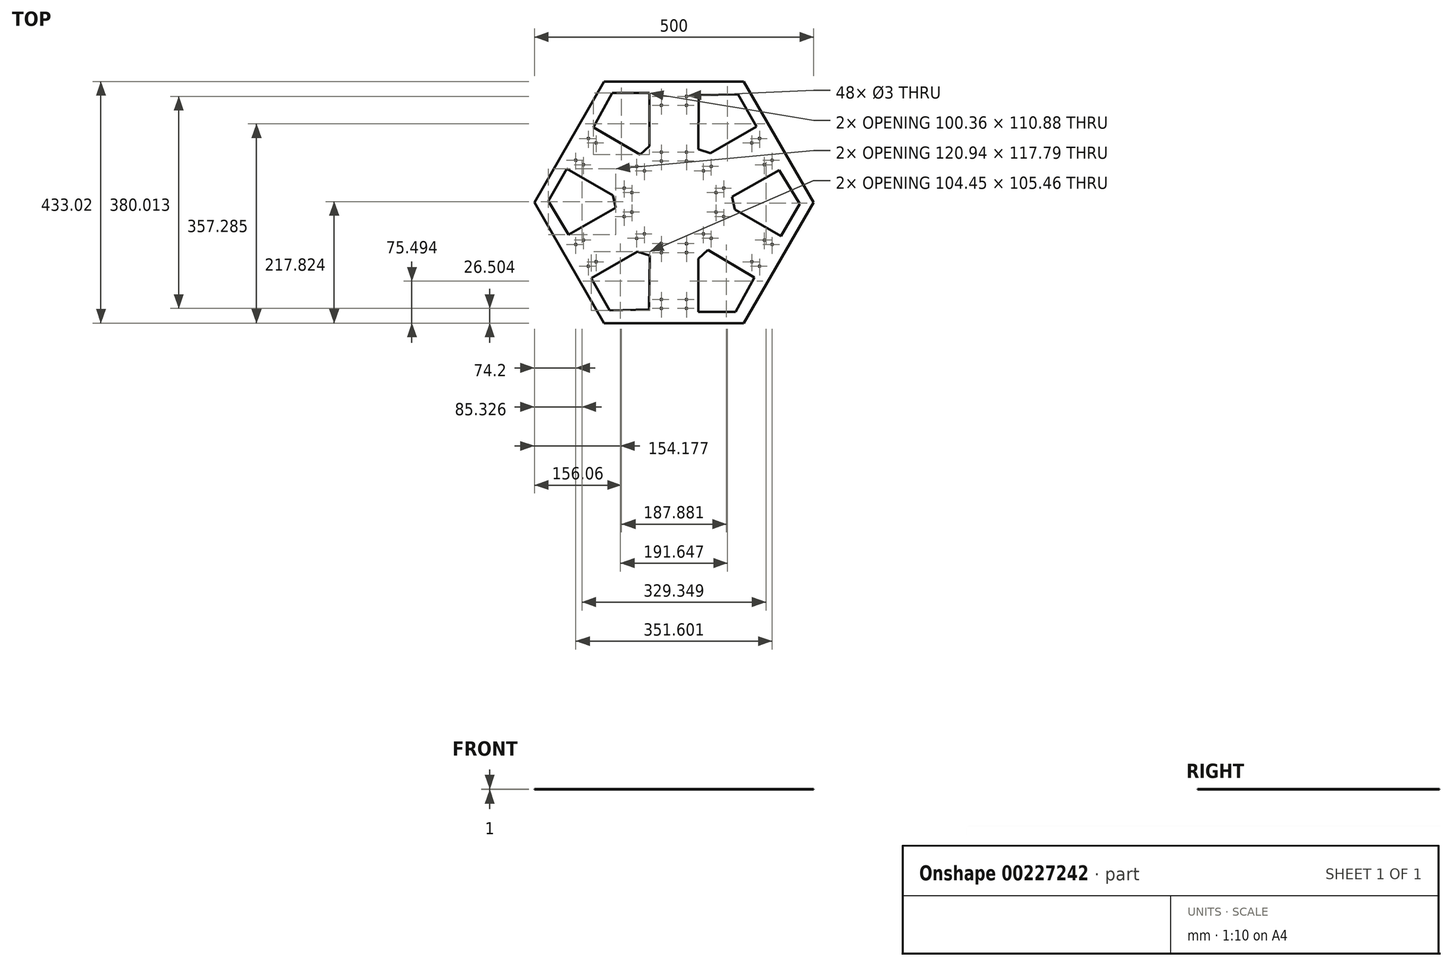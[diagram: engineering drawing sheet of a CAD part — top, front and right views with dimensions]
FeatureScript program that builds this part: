
annotation { "Feature Type Name" : "Feature", "Feature Type Description" : "" }
export const myFeature = defineFeature(function(context is Context, id is Id, definition is map)
    precondition{}
    {
        {
            var Q0;
            Q0=qCreatedBy(makeId("Top.planeOp"),FACE);
            var sketch = newSketch(context, id + "F0", { "sketchPlane" : qUnion([Q0])});
            skCircle(sketch, "E0.cCircle", {"center": v(0, 0) * mm, "radius": 250 * mm, "construction": true});
            skLineSegment(sketch, "E0.0", {"start": v(250, 0) * mm, "end": v(125, -216.5) * mm});
            skLineSegment(sketch, "E0.1", {"start": v(125, -216.5) * mm, "end": v(-125, -216.5) * mm});
            skLineSegment(sketch, "E0.2", {"start": v(-125, -216.5) * mm, "end": v(-250, 0) * mm});
            skLineSegment(sketch, "E0.3", {"start": v(-250, 0) * mm, "end": v(-125, 216.5) * mm});
            skLineSegment(sketch, "E0.4", {"start": v(-125, 216.5) * mm, "end": v(125, 216.5) * mm});
            skLineSegment(sketch, "E0.5", {"start": v(125, 216.5) * mm, "end": v(250, 0) * mm});
            skCircle(sketch, "E1", {"center": v(-22.5, 190) * mm, "radius": 1.5 * mm});
            skCircle(sketch, "E2.MirrorC", {"center": v(22.5, 190) * mm, "radius": 1.5 * mm});
            skCircle(sketch, "E3.0.1.0", {"center": v(-22.5, 174) * mm, "radius": 1.5 * mm});
            skCircle(sketch, "E3.0.1.1", {"center": v(22.5, 174) * mm, "radius": 1.5 * mm});
            skLineSegment(sketch, "E3.direction1", {"start": v(-22.5, 190) * mm, "end": v(2.5, 190) * mm, "construction": true});
            skLineSegment(sketch, "E3.direction2", {"start": v(-22.5, 190) * mm, "end": v(-22.5, 174) * mm, "construction": true});
            skCircle(sketch, "E4.0.1.0", {"center": v(22.5, 90) * mm, "radius": 1.5 * mm});
            skCircle(sketch, "E4.0.1.1", {"center": v(-22.5, 74) * mm, "radius": 1.5 * mm});
            skCircle(sketch, "E4.0.1.2", {"center": v(22.5, 74) * mm, "radius": 1.5 * mm});
            skLineSegment(sketch, "E4.0.1.3", {"start": v(-22.5, 90) * mm, "end": v(2.5, 90) * mm, "construction": true});
            skLineSegment(sketch, "E4.0.1.4", {"start": v(-22.5, 90) * mm, "end": v(-22.5, 74) * mm, "construction": true});
            skCircle(sketch, "E4.0.1.5", {"center": v(-22.5, 90) * mm, "radius": 1.5 * mm});
            skLineSegment(sketch, "E4.direction1", {"start": v(-22.5, 174) * mm, "end": v(2.5, 174) * mm, "construction": true});
            skLineSegment(sketch, "E4.direction2", {"start": v(-22.5, 174) * mm, "end": v(-22.5, 74) * mm, "construction": true});
            skLineSegment(sketch, "E5.1.0", {"start": v(-175.8, 75.52) * mm, "end": v(-163.3, 97.17) * mm, "construction": true});
            skLineSegment(sketch, "E5.1.1", {"start": v(-175.8, 75.52) * mm, "end": v(-161.94, 67.52) * mm, "construction": true});
            skLineSegment(sketch, "E5.1.2", {"start": v(-161.94, 67.52) * mm, "end": v(-75.34, 17.52) * mm, "construction": true});
            skLineSegment(sketch, "E5.1.3", {"start": v(-89.2, 25.52) * mm, "end": v(-76.7, 47.17) * mm, "construction": true});
            skLineSegment(sketch, "E5.1.4", {"start": v(-161.94, 67.52) * mm, "end": v(-149.44, 89.17) * mm, "construction": true});
            skCircle(sketch, "E5.1.5", {"center": v(-66.7, 64.49) * mm, "radius": 1.5 * mm});
            skLineSegment(sketch, "E5.1.6", {"start": v(-89.2, 25.52) * mm, "end": v(-75.34, 17.52) * mm, "construction": true});
            skCircle(sketch, "E5.1.7", {"center": v(-52.84, 56.49) * mm, "radius": 1.5 * mm});
            skCircle(sketch, "E5.1.8", {"center": v(-153.3, 114.49) * mm, "radius": 1.5 * mm});
            skCircle(sketch, "E5.1.9", {"center": v(-139.44, 106.49) * mm, "radius": 1.5 * mm});
            skCircle(sketch, "E5.1.10", {"center": v(-75.34, 17.52) * mm, "radius": 1.5 * mm});
            skCircle(sketch, "E5.1.11", {"center": v(-175.8, 75.52) * mm, "radius": 1.5 * mm});
            skCircle(sketch, "E5.1.12", {"center": v(-89.2, 25.52) * mm, "radius": 1.5 * mm});
            skCircle(sketch, "E5.1.13", {"center": v(-161.94, 67.52) * mm, "radius": 1.5 * mm});
            skLineSegment(sketch, "E5.2.0", {"start": v(-153.3, -114.49) * mm, "end": v(-165.8, -92.84) * mm, "construction": true});
            skLineSegment(sketch, "E5.2.1", {"start": v(-153.3, -114.49) * mm, "end": v(-139.44, -106.49) * mm, "construction": true});
            skLineSegment(sketch, "E5.2.2", {"start": v(-139.44, -106.49) * mm, "end": v(-52.84, -56.49) * mm, "construction": true});
            skLineSegment(sketch, "E5.2.3", {"start": v(-66.7, -64.49) * mm, "end": v(-79.2, -42.84) * mm, "construction": true});
            skLineSegment(sketch, "E5.2.4", {"start": v(-139.44, -106.49) * mm, "end": v(-151.94, -84.84) * mm, "construction": true});
            skCircle(sketch, "E5.2.5", {"center": v(-89.2, -25.52) * mm, "radius": 1.5 * mm});
            skLineSegment(sketch, "E5.2.6", {"start": v(-66.7, -64.49) * mm, "end": v(-52.84, -56.49) * mm, "construction": true});
            skCircle(sketch, "E5.2.7", {"center": v(-75.34, -17.52) * mm, "radius": 1.5 * mm});
            skCircle(sketch, "E5.2.8", {"center": v(-175.8, -75.52) * mm, "radius": 1.5 * mm});
            skCircle(sketch, "E5.2.9", {"center": v(-161.94, -67.52) * mm, "radius": 1.5 * mm});
            skCircle(sketch, "E5.2.10", {"center": v(-52.84, -56.49) * mm, "radius": 1.5 * mm});
            skCircle(sketch, "E5.2.11", {"center": v(-153.3, -114.49) * mm, "radius": 1.5 * mm});
            skCircle(sketch, "E5.2.12", {"center": v(-66.7, -64.49) * mm, "radius": 1.5 * mm});
            skCircle(sketch, "E5.2.13", {"center": v(-139.44, -106.49) * mm, "radius": 1.5 * mm});
            skLineSegment(sketch, "E5.3.0", {"start": v(22.5, -190) * mm, "end": v(-2.5, -190) * mm, "construction": true});
            skLineSegment(sketch, "E5.3.1", {"start": v(22.5, -190) * mm, "end": v(22.5, -174) * mm, "construction": true});
            skLineSegment(sketch, "E5.3.2", {"start": v(22.5, -174) * mm, "end": v(22.5, -74) * mm, "construction": true});
            skLineSegment(sketch, "E5.3.3", {"start": v(22.5, -90) * mm, "end": v(-2.5, -90) * mm, "construction": true});
            skLineSegment(sketch, "E5.3.4", {"start": v(22.5, -174) * mm, "end": v(-2.5, -174) * mm, "construction": true});
            skCircle(sketch, "E5.3.5", {"center": v(-22.5, -90) * mm, "radius": 1.5 * mm});
            skLineSegment(sketch, "E5.3.6", {"start": v(22.5, -90) * mm, "end": v(22.5, -74) * mm, "construction": true});
            skCircle(sketch, "E5.3.7", {"center": v(-22.5, -74) * mm, "radius": 1.5 * mm});
            skCircle(sketch, "E5.3.8", {"center": v(-22.5, -190) * mm, "radius": 1.5 * mm});
            skCircle(sketch, "E5.3.9", {"center": v(-22.5, -174) * mm, "radius": 1.5 * mm});
            skCircle(sketch, "E5.3.10", {"center": v(22.5, -74) * mm, "radius": 1.5 * mm});
            skCircle(sketch, "E5.3.11", {"center": v(22.5, -190) * mm, "radius": 1.5 * mm});
            skCircle(sketch, "E5.3.12", {"center": v(22.5, -90) * mm, "radius": 1.5 * mm});
            skCircle(sketch, "E5.3.13", {"center": v(22.5, -174) * mm, "radius": 1.5 * mm});
            skLineSegment(sketch, "E5.4.0", {"start": v(175.8, -75.52) * mm, "end": v(163.3, -97.17) * mm, "construction": true});
            skLineSegment(sketch, "E5.4.1", {"start": v(175.8, -75.52) * mm, "end": v(161.94, -67.52) * mm, "construction": true});
            skLineSegment(sketch, "E5.4.2", {"start": v(161.94, -67.52) * mm, "end": v(75.34, -17.52) * mm, "construction": true});
            skLineSegment(sketch, "E5.4.3", {"start": v(89.2, -25.52) * mm, "end": v(76.7, -47.17) * mm, "construction": true});
            skLineSegment(sketch, "E5.4.4", {"start": v(161.94, -67.52) * mm, "end": v(149.44, -89.17) * mm, "construction": true});
            skCircle(sketch, "E5.4.5", {"center": v(66.7, -64.49) * mm, "radius": 1.5 * mm});
            skLineSegment(sketch, "E5.4.6", {"start": v(89.2, -25.52) * mm, "end": v(75.34, -17.52) * mm, "construction": true});
            skCircle(sketch, "E5.4.7", {"center": v(52.84, -56.49) * mm, "radius": 1.5 * mm});
            skCircle(sketch, "E5.4.8", {"center": v(153.3, -114.49) * mm, "radius": 1.5 * mm});
            skCircle(sketch, "E5.4.9", {"center": v(139.44, -106.49) * mm, "radius": 1.5 * mm});
            skCircle(sketch, "E5.4.10", {"center": v(75.34, -17.52) * mm, "radius": 1.5 * mm});
            skCircle(sketch, "E5.4.11", {"center": v(175.8, -75.52) * mm, "radius": 1.5 * mm});
            skCircle(sketch, "E5.4.12", {"center": v(89.2, -25.52) * mm, "radius": 1.5 * mm});
            skCircle(sketch, "E5.4.13", {"center": v(161.94, -67.52) * mm, "radius": 1.5 * mm});
            skLineSegment(sketch, "E5.5.0", {"start": v(153.3, 114.49) * mm, "end": v(165.8, 92.84) * mm, "construction": true});
            skLineSegment(sketch, "E5.5.1", {"start": v(153.3, 114.49) * mm, "end": v(139.44, 106.49) * mm, "construction": true});
            skLineSegment(sketch, "E5.5.2", {"start": v(139.44, 106.49) * mm, "end": v(52.84, 56.49) * mm, "construction": true});
            skLineSegment(sketch, "E5.5.3", {"start": v(66.7, 64.49) * mm, "end": v(79.2, 42.84) * mm, "construction": true});
            skLineSegment(sketch, "E5.5.4", {"start": v(139.44, 106.49) * mm, "end": v(151.94, 84.84) * mm, "construction": true});
            skCircle(sketch, "E5.5.5", {"center": v(89.2, 25.52) * mm, "radius": 1.5 * mm});
            skLineSegment(sketch, "E5.5.6", {"start": v(66.7, 64.49) * mm, "end": v(52.84, 56.49) * mm, "construction": true});
            skCircle(sketch, "E5.5.7", {"center": v(75.34, 17.52) * mm, "radius": 1.5 * mm});
            skCircle(sketch, "E5.5.8", {"center": v(175.8, 75.52) * mm, "radius": 1.5 * mm});
            skCircle(sketch, "E5.5.9", {"center": v(161.94, 67.52) * mm, "radius": 1.5 * mm});
            skCircle(sketch, "E5.5.10", {"center": v(52.84, 56.49) * mm, "radius": 1.5 * mm});
            skCircle(sketch, "E5.5.11", {"center": v(153.3, 114.49) * mm, "radius": 1.5 * mm});
            skCircle(sketch, "E5.5.12", {"center": v(66.7, 64.49) * mm, "radius": 1.5 * mm});
            skCircle(sketch, "E5.5.13", {"center": v(139.44, 106.49) * mm, "radius": 1.5 * mm});
            skSolve(sketch);
        }
        {
            var Q0;
            Q0=makeQuery(id+"F0.imprint","IMPRINT",FACE,{"disambiguationData":[TD([[makeQuery(id+"F0.imprint","IMPRINT",EDGE,{"derivedFrom":sQuery(id+"F0.wireOp",EDGE,"E0.0")}),-1.0]])]});
            extrude(context, id + "F1", {"entities" : qUnion([Q0]), "depth" : 1 * mm});
        }
        {
            var Q0;
            Q0=makeQuery(id+"F1.opExtrude","CAP_FACE",FACE,{"disambiguationData":[OSD([sQuery(id+"F0.wireOp",EDGE,"E0.0"),sQuery(id+"F0.wireOp",EDGE,"E0.1"),sQuery(id+"F0.wireOp",EDGE,"E0.2"),sQuery(id+"F0.wireOp",EDGE,"E0.3"),sQuery(id+"F0.wireOp",EDGE,"E0.4"),sQuery(id+"F0.wireOp",EDGE,"E0.5"),sQuery(id+"F0.wireOp",EDGE,"E1"),sQuery(id+"F0.wireOp",EDGE,"E2.MirrorC"),sQuery(id+"F0.wireOp",EDGE,"E3.0.1.0"),sQuery(id+"F0.wireOp",EDGE,"E3.0.1.1"),sQuery(id+"F0.wireOp",EDGE,"E4.0.1.0"),sQuery(id+"F0.wireOp",EDGE,"E4.0.1.1"),sQuery(id+"F0.wireOp",EDGE,"E4.0.1.2"),sQuery(id+"F0.wireOp",EDGE,"E4.0.1.5"),sQuery(id+"F0.wireOp",EDGE,"E5.1.5"),sQuery(id+"F0.wireOp",EDGE,"E5.1.7"),sQuery(id+"F0.wireOp",EDGE,"E5.1.8"),sQuery(id+"F0.wireOp",EDGE,"E5.1.9"),sQuery(id+"F0.wireOp",EDGE,"E5.1.10"),sQuery(id+"F0.wireOp",EDGE,"E5.1.11"),sQuery(id+"F0.wireOp",EDGE,"E5.1.12"),sQuery(id+"F0.wireOp",EDGE,"E5.1.13"),sQuery(id+"F0.wireOp",EDGE,"E5.2.5"),sQuery(id+"F0.wireOp",EDGE,"E5.2.7"),sQuery(id+"F0.wireOp",EDGE,"E5.2.8"),sQuery(id+"F0.wireOp",EDGE,"E5.2.9"),sQuery(id+"F0.wireOp",EDGE,"E5.2.10"),sQuery(id+"F0.wireOp",EDGE,"E5.2.11"),sQuery(id+"F0.wireOp",EDGE,"E5.2.12"),sQuery(id+"F0.wireOp",EDGE,"E5.2.13"),sQuery(id+"F0.wireOp",EDGE,"E5.3.5"),sQuery(id+"F0.wireOp",EDGE,"E5.3.7"),sQuery(id+"F0.wireOp",EDGE,"E5.3.8"),sQuery(id+"F0.wireOp",EDGE,"E5.3.9"),sQuery(id+"F0.wireOp",EDGE,"E5.3.10"),sQuery(id+"F0.wireOp",EDGE,"E5.3.11"),sQuery(id+"F0.wireOp",EDGE,"E5.3.12"),sQuery(id+"F0.wireOp",EDGE,"E5.3.13"),sQuery(id+"F0.wireOp",EDGE,"E5.4.5"),sQuery(id+"F0.wireOp",EDGE,"E5.4.7"),sQuery(id+"F0.wireOp",EDGE,"E5.4.8"),sQuery(id+"F0.wireOp",EDGE,"E5.4.9"),sQuery(id+"F0.wireOp",EDGE,"E5.4.10"),sQuery(id+"F0.wireOp",EDGE,"E5.4.11"),sQuery(id+"F0.wireOp",EDGE,"E5.4.12"),sQuery(id+"F0.wireOp",EDGE,"E5.4.13"),sQuery(id+"F0.wireOp",EDGE,"E5.5.5"),sQuery(id+"F0.wireOp",EDGE,"E5.5.7"),sQuery(id+"F0.wireOp",EDGE,"E5.5.8"),sQuery(id+"F0.wireOp",EDGE,"E5.5.9"),sQuery(id+"F0.wireOp",EDGE,"E5.5.10"),sQuery(id+"F0.wireOp",EDGE,"E5.5.11"),sQuery(id+"F0.wireOp",EDGE,"E5.5.12"),sQuery(id+"F0.wireOp",EDGE,"E5.5.13")])],"isStart":false});
            var sketch = newSketch(context, id + "F2", { "sketchPlane" : qUnion([Q0])});
            skLineSegment(sketch, "E6", {"start": v(-144.12, 134.46) * mm, "end": v(-110.43, 196.22) * mm});
            skLineSegment(sketch, "E7", {"start": v(-110.43, 196.22) * mm, "end": v(-43.76, 196.22) * mm});
            skLineSegment(sketch, "E8", {"start": v(-43.76, 196.22) * mm, "end": v(-43.76, 100.77) * mm});
            skLineSegment(sketch, "E9", {"start": v(-43.76, 100.77) * mm, "end": v(-60.6, 85.33) * mm});
            skLineSegment(sketch, "E10", {"start": v(-60.6, 85.33) * mm, "end": v(-144.12, 134.46) * mm});
            skLineSegment(sketch, "E11.1.0", {"start": v(-188.5, -57.58) * mm, "end": v(-225.15, 2.47) * mm});
            skLineSegment(sketch, "E11.1.1", {"start": v(-225.15, 2.47) * mm, "end": v(-191.81, 60.2) * mm});
            skLineSegment(sketch, "E11.1.2", {"start": v(-191.81, 60.2) * mm, "end": v(-109.15, 12.49) * mm});
            skLineSegment(sketch, "E11.1.3", {"start": v(-104.2, -9.82) * mm, "end": v(-188.5, -57.58) * mm});
            skLineSegment(sketch, "E11.1.4", {"start": v(-109.15, 12.49) * mm, "end": v(-104.2, -9.82) * mm});
            skLineSegment(sketch, "E11.2.0", {"start": v(-44.39, -192.04) * mm, "end": v(-114.71, -193.75) * mm});
            skLineSegment(sketch, "E11.2.1", {"start": v(-114.71, -193.75) * mm, "end": v(-148.05, -136) * mm});
            skLineSegment(sketch, "E11.2.2", {"start": v(-148.05, -136) * mm, "end": v(-65.4, -88.29) * mm});
            skLineSegment(sketch, "E11.2.3", {"start": v(-43.6, -95.15) * mm, "end": v(-44.39, -192.04) * mm});
            skLineSegment(sketch, "E11.2.4", {"start": v(-65.4, -88.29) * mm, "end": v(-43.6, -95.15) * mm});
            skLineSegment(sketch, "E11.3.0", {"start": v(144.12, -134.46) * mm, "end": v(110.43, -196.22) * mm});
            skLineSegment(sketch, "E11.3.1", {"start": v(110.43, -196.22) * mm, "end": v(43.76, -196.22) * mm});
            skLineSegment(sketch, "E11.3.2", {"start": v(43.76, -196.22) * mm, "end": v(43.76, -100.77) * mm});
            skLineSegment(sketch, "E11.3.3", {"start": v(60.6, -85.33) * mm, "end": v(144.12, -134.46) * mm});
            skLineSegment(sketch, "E11.3.4", {"start": v(43.76, -100.77) * mm, "end": v(60.6, -85.33) * mm});
            skLineSegment(sketch, "E11.4.0", {"start": v(188.5, 57.58) * mm, "end": v(225.15, -2.47) * mm});
            skLineSegment(sketch, "E11.4.1", {"start": v(225.15, -2.47) * mm, "end": v(191.81, -60.2) * mm});
            skLineSegment(sketch, "E11.4.2", {"start": v(191.81, -60.2) * mm, "end": v(109.15, -12.49) * mm});
            skLineSegment(sketch, "E11.4.3", {"start": v(104.2, 9.82) * mm, "end": v(188.5, 57.58) * mm});
            skLineSegment(sketch, "E11.4.4", {"start": v(109.15, -12.49) * mm, "end": v(104.2, 9.82) * mm});
            skLineSegment(sketch, "E11.5.0", {"start": v(44.39, 192.04) * mm, "end": v(114.71, 193.75) * mm});
            skLineSegment(sketch, "E11.5.1", {"start": v(114.71, 193.75) * mm, "end": v(148.05, 136) * mm});
            skLineSegment(sketch, "E11.5.2", {"start": v(148.05, 136) * mm, "end": v(65.4, 88.29) * mm});
            skLineSegment(sketch, "E11.5.3", {"start": v(43.6, 95.15) * mm, "end": v(44.39, 192.04) * mm});
            skLineSegment(sketch, "E11.5.4", {"start": v(65.4, 88.29) * mm, "end": v(43.6, 95.15) * mm});
            skPoint(sketch, "E11.center", {"position": v(0, 0) * mm});
            skSolve(sketch);
        }
        {
            var Q0;
            Q0 = qSketchRegion(id + "F2", true);
            extrude(context, id + "F3", {"entities" : qUnion([Q0]), "operationType" : NewBodyOperationType.REMOVE, "oppositeDirection" : true, "depth" : 25 * mm});
        }
    });
